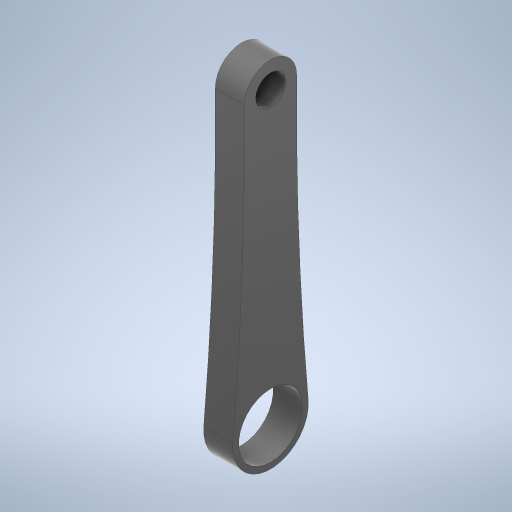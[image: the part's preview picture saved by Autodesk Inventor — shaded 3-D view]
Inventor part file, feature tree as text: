
AUTODESK INVENTOR PART (.ipt)
format: ipt  version: 2023 (Build 270158000, 158)  size: 266,240 bytes
history: native  units: mm
features: extrude x1, plane x1, sketch x1
ambient origin geometry x8: Origin, YZ Plane, XZ Plane, XY Plane, X Axis, Y Axis, Z Axis, Center Point
bodies: Volumenkörper1 (feature_tree)
feature tree (3):
  extrude  "Extrusion1"  Depth=99.913mm
  plane  "Arbeitsebene1"
  sketch  "Skizze1"  dims[d0=26.0mm d1=99.913mm d2=21.9mm d3=18.0mm d6=0.0mm d7=0.0mm d8=0.0mm d9=10.0mm d10=10.0mm d11=10.2mm d12=10.0mm d13=0.0mm d14=0.0mm]
